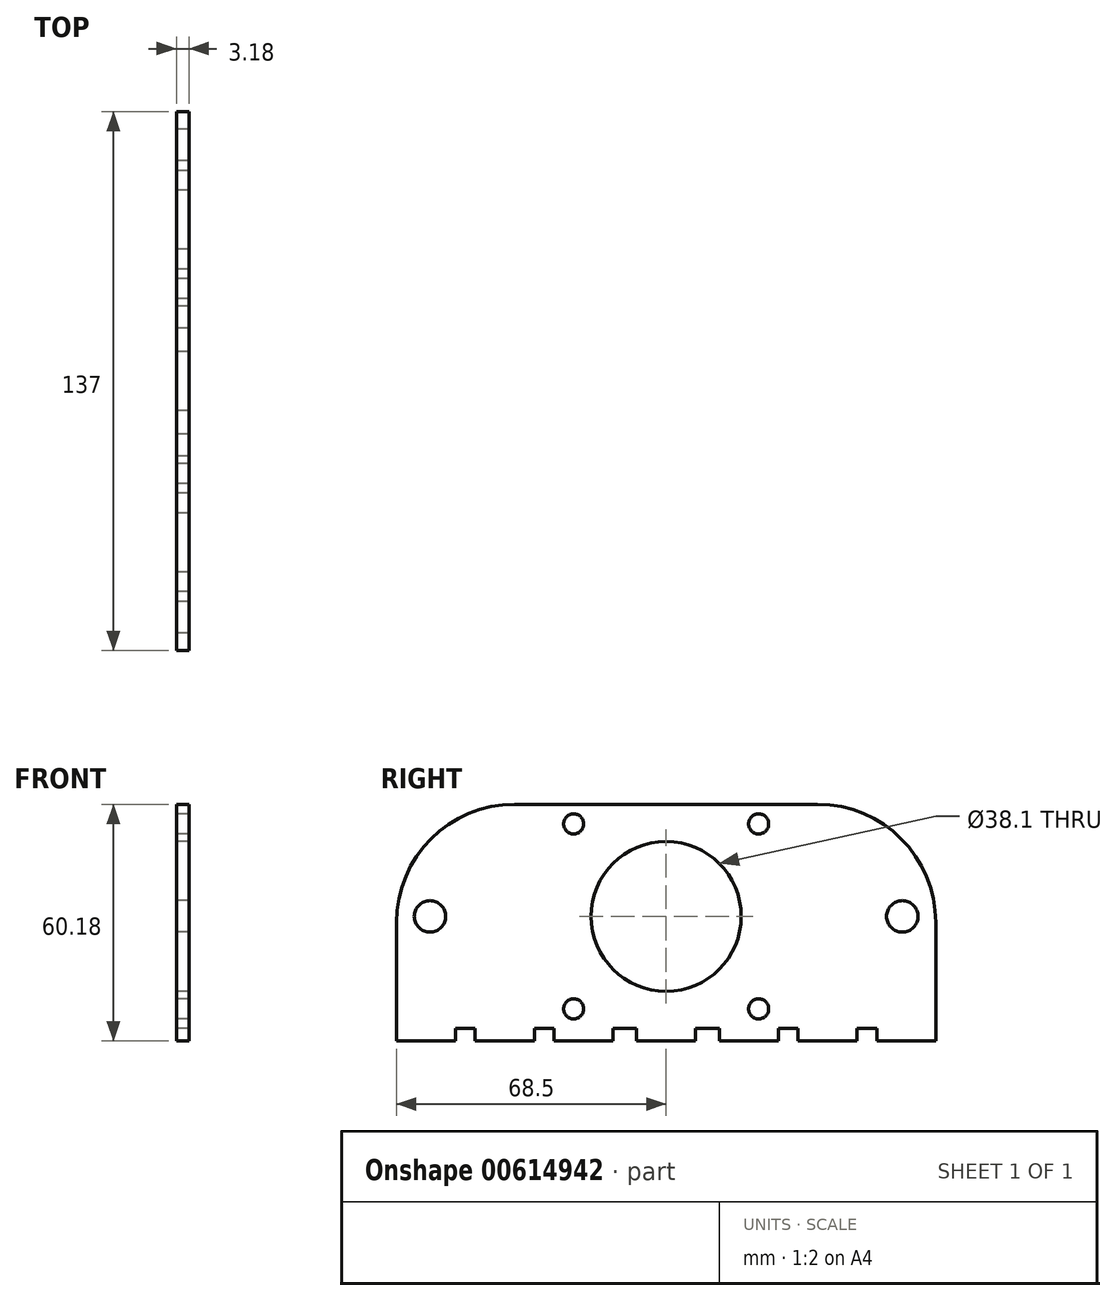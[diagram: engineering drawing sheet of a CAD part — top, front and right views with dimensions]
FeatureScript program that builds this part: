
annotation { "Feature Type Name" : "Feature", "Feature Type Description" : "" }
export const myFeature = defineFeature(function(context is Context, id is Id, definition is map)
    precondition{}
    {
        {
            var Q0;
            Q0=qCreatedBy(makeId("Right.planeOp"),FACE);
            var sketch = newSketch(context, id + "F0", { "sketchPlane" : qUnion([Q0])});
            skLineSegment(sketch, "E0.bottom", {"start": v(-28.5, 28.5) * mm, "end": v(28.5, 28.5) * mm});
            skLineSegment(sketch, "E0.top", {"start": v(-28.5, -28.5) * mm, "end": v(28.5, -28.5) * mm});
            skLineSegment(sketch, "E0.left", {"start": v(-28.5, 28.5) * mm, "end": v(-28.5, -28.5) * mm});
            skLineSegment(sketch, "E0.right", {"start": v(28.5, 28.5) * mm, "end": v(28.5, -28.5) * mm});
            skPoint(sketch, "E0.middle", {"position": v(0, 0) * mm});
            skLineSegment(sketch, "E1.bottom", {"start": v(28.5, -28.5) * mm, "end": v(13.5, -28.5) * mm});
            skLineSegment(sketch, "E1.top", {"start": v(28.5, -31.68) * mm, "end": v(13.5, -31.68) * mm});
            skLineSegment(sketch, "E1.left", {"start": v(28.5, -28.5) * mm, "end": v(28.5, -31.68) * mm});
            skLineSegment(sketch, "E1.right", {"start": v(13.5, -28.5) * mm, "end": v(13.5, -31.67) * mm});
            skLineSegment(sketch, "E2.bottom", {"start": v(-28.5, -28.5) * mm, "end": v(-13.5, -28.5) * mm});
            skLineSegment(sketch, "E2.top", {"start": v(-28.5, -31.67) * mm, "end": v(-13.5, -31.67) * mm});
            skLineSegment(sketch, "E2.left", {"start": v(-28.5, -28.5) * mm, "end": v(-28.5, -31.67) * mm});
            skLineSegment(sketch, "E2.right", {"start": v(-13.5, -28.5) * mm, "end": v(-13.5, -31.67) * mm});
            skLineSegment(sketch, "E3.bottom", {"start": v(0, -28.5) * mm, "end": v(7.5, -28.5) * mm});
            skLineSegment(sketch, "E3.top", {"start": v(0, -31.67) * mm, "end": v(7.5, -31.67) * mm});
            skLineSegment(sketch, "E3.left", {"start": v(0, -28.5) * mm, "end": v(0, -31.67) * mm});
            skLineSegment(sketch, "E3.right", {"start": v(7.5, -28.5) * mm, "end": v(7.5, -31.67) * mm});
            skLineSegment(sketch, "E4.bottom", {"start": v(0, -31.67) * mm, "end": v(-7.5, -31.67) * mm});
            skLineSegment(sketch, "E4.top", {"start": v(0, -28.5) * mm, "end": v(-7.5, -28.5) * mm});
            skLineSegment(sketch, "E4.left", {"start": v(0, -31.67) * mm, "end": v(0, -28.5) * mm});
            skLineSegment(sketch, "E4.right", {"start": v(-7.5, -31.67) * mm, "end": v(-7.5, -28.5) * mm});
            skCircle(sketch, "E5", {"center": v(0, 0) * mm, "radius": 19.05 * mm});
            skLineSegment(sketch, "E6.bottom", {"start": v(-23.5, 23.5) * mm, "end": v(23.5, 23.5) * mm});
            skLineSegment(sketch, "E6.top", {"start": v(-23.5, -23.5) * mm, "end": v(23.5, -23.5) * mm});
            skLineSegment(sketch, "E6.left", {"start": v(-23.5, 23.5) * mm, "end": v(-23.5, -23.5) * mm});
            skLineSegment(sketch, "E6.right", {"start": v(23.5, 23.5) * mm, "end": v(23.5, -23.5) * mm});
            skCircle(sketch, "E7", {"center": v(23.5, 23.5) * mm, "radius": 2.55 * mm});
            skCircle(sketch, "E8.MirrorC", {"center": v(-23.5, 23.5) * mm, "radius": 2.55 * mm});
            skCircle(sketch, "E9.MirrorC", {"center": v(-23.5, -23.5) * mm, "radius": 2.55 * mm});
            skCircle(sketch, "E10.MirrorC", {"center": v(23.5, -23.5) * mm, "radius": 2.55 * mm});
            skLineSegment(sketch, "E11.bottom", {"start": v(-28.5, 28.5) * mm, "end": v(-38.5, 28.5) * mm});
            skLineSegment(sketch, "E11.top", {"start": v(-28.5, -28.5) * mm, "end": v(-68.5, -28.5) * mm});
            skLineSegment(sketch, "E11.right", {"start": v(-68.5, -1.5) * mm, "end": v(-68.5, -28.5) * mm});
            skLineSegment(sketch, "E12", {"start": v(0, 0) * mm, "end": v(-60, 0) * mm});
            skCircle(sketch, "E13", {"center": v(-60, 0) * mm, "radius": 4 * mm});
            skPoint(sketch, "E14.visualSharp", {"position": v(-68.5, 28.5) * mm});
            skArc(sketch, "E14.filletArc", {"start": v(-38.5, 28.5) * mm, "mid": v(-59.71, 19.71) * mm, "end": v(-68.5, -1.5) * mm});
            skLineSegment(sketch, "E15.bottom", {"start": v(-68.5, -28.5) * mm, "end": v(-53.5, -28.5) * mm});
            skLineSegment(sketch, "E15.top", {"start": v(-68.5, -31.68) * mm, "end": v(-53.5, -31.68) * mm});
            skLineSegment(sketch, "E15.left", {"start": v(-68.5, -28.5) * mm, "end": v(-68.5, -31.68) * mm});
            skLineSegment(sketch, "E15.right", {"start": v(-53.5, -28.5) * mm, "end": v(-53.5, -31.68) * mm});
            skLineSegment(sketch, "E16", {"start": v(-53.5, -28.5) * mm, "end": v(-28.5, -28.5) * mm});
            skLineSegment(sketch, "E17.bottom", {"start": v(-41, -28.5) * mm, "end": v(-48.5, -28.5) * mm});
            skLineSegment(sketch, "E17.top", {"start": v(-41, -31.68) * mm, "end": v(-48.5, -31.68) * mm});
            skLineSegment(sketch, "E17.left", {"start": v(-41, -28.5) * mm, "end": v(-41, -31.68) * mm});
            skLineSegment(sketch, "E17.right", {"start": v(-48.5, -28.5) * mm, "end": v(-48.5, -31.68) * mm});
            skLineSegment(sketch, "E18.bottom", {"start": v(-41, -28.5) * mm, "end": v(-33.5, -28.5) * mm});
            skLineSegment(sketch, "E18.top", {"start": v(-41, -31.68) * mm, "end": v(-33.5, -31.68) * mm});
            skLineSegment(sketch, "E18.right", {"start": v(-33.5, -28.5) * mm, "end": v(-33.5, -31.68) * mm});
            skLineSegment(sketch, "E19.MirrorCS", {"start": v(28.5, 28.5) * mm, "end": v(38.5, 28.5) * mm});
            skCircle(sketch, "E20.MirrorC", {"center": v(60, 0) * mm, "radius": 4 * mm});
            skArc(sketch, "E21.MirrorCS", {"start": v(38.5, 28.5) * mm, "mid": v(59.71, 19.71) * mm, "end": v(68.5, -1.5) * mm});
            skLineSegment(sketch, "E22.MirrorCS", {"start": v(68.5, -1.5) * mm, "end": v(68.5, -28.5) * mm});
            skLineSegment(sketch, "E23.MirrorCS", {"start": v(28.5, -28.5) * mm, "end": v(68.5, -28.5) * mm});
            skLineSegment(sketch, "E24.MirrorCS", {"start": v(33.5, -28.5) * mm, "end": v(33.5, -31.68) * mm});
            skLineSegment(sketch, "E25.MirrorCS", {"start": v(41, -31.68) * mm, "end": v(33.5, -31.68) * mm});
            skLineSegment(sketch, "E26.MirrorCS", {"start": v(41, -31.68) * mm, "end": v(48.5, -31.68) * mm});
            skLineSegment(sketch, "E27.MirrorCS", {"start": v(48.5, -28.5) * mm, "end": v(48.5, -31.68) * mm});
            skLineSegment(sketch, "E28.MirrorCS", {"start": v(53.5, -28.5) * mm, "end": v(53.5, -31.68) * mm});
            skLineSegment(sketch, "E29.MirrorCS", {"start": v(68.5, -31.68) * mm, "end": v(53.5, -31.68) * mm});
            skLineSegment(sketch, "E30.MirrorCS", {"start": v(68.5, -28.5) * mm, "end": v(68.5, -31.68) * mm});
            skSolve(sketch);
        }
        {
            var Q0;
            Q0 = qSketchRegion(id + "F0", true);
            var Q1;
            Q1=makeQuery(id+"F0.imprint","IMPRINT",FACE,{"disambiguationData":[TD([[makeQuery(id+"F0.imprint","IMPRINT",EDGE,{"derivedFrom":sQuery(id+"F0.wireOp",EDGE,"E5")}),-1.0]])]});
            extrude(context, id + "F1", {"entities" : qUnion([Q0, Q1]), "depth" : 3.17 * mm, "offsetDistance" : 25 * mm});
        }
    });
